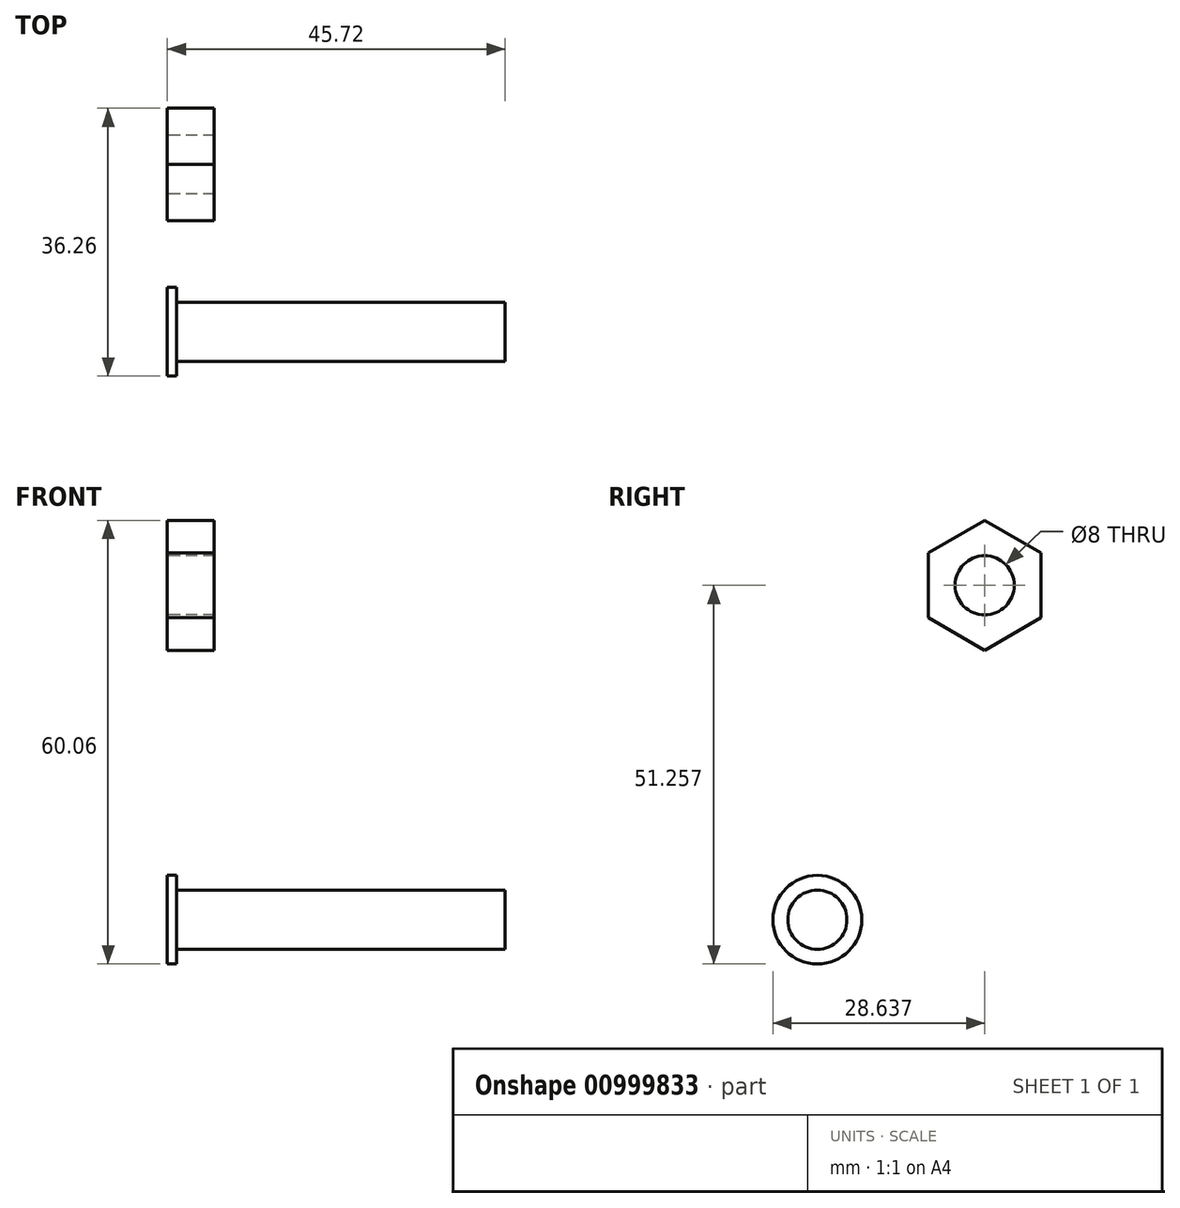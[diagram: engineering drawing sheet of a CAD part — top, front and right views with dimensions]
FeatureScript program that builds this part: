
annotation { "Feature Type Name" : "Feature", "Feature Type Description" : "" }
export const myFeature = defineFeature(function(context is Context, id is Id, definition is map)
    precondition{}
    {
        {
            var Q0;
            Q0=qCreatedBy(makeId("Right.planeOp"),FACE);
            var sketch = newSketch(context, id + "F0", { "sketchPlane" : qUnion([Q0])});
            skCircle(sketch, "E0", {"center": v(0, 0) * mm, "radius": 4 * mm});
            skCircle(sketch, "E1", {"center": v(0, 0) * mm, "radius": 6 * mm});
            skSolve(sketch);
        }
        {
            var Q0;
            Q0=makeQuery(id+"F0.imprint","IMPRINT",FACE,{"disambiguationData":[TD([[makeQuery(id+"F0.imprint","IMPRINT",EDGE,{"derivedFrom":sQuery(id+"F0.wireOp",EDGE,"E0")}),1.0]])]});
            extrude(context, id + "F1", {"entities" : qUnion([Q0]), "depth" : 45.72 * mm, "offsetDistance" : 25.4 * mm});
        }
        {
            var Q0;
            Q0 = qSketchRegion(id + "F0", true);
            extrude(context, id + "F2", {"entities" : qUnion([Q0]), "operationType" : NewBodyOperationType.ADD, "depth" : 1.27 * mm, "offsetDistance" : 25.4 * mm});
        }
        {
            var Q0;
            Q0=qCreatedBy(makeId("Right.planeOp"),FACE);
            var sketch = newSketch(context, id + "F3", { "sketchPlane" : qUnion([Q0])});
            skCircle(sketch, "E2.cCircle", {"center": v(22.64, 45.26) * mm, "radius": 7.62 * mm, "construction": true});
            skLineSegment(sketch, "E2.0", {"start": v(30.26, 49.66) * mm, "end": v(30.26, 40.86) * mm});
            skLineSegment(sketch, "E2.1", {"start": v(30.26, 40.86) * mm, "end": v(22.64, 36.46) * mm});
            skLineSegment(sketch, "E2.2", {"start": v(22.64, 36.46) * mm, "end": v(15.02, 40.86) * mm});
            skLineSegment(sketch, "E2.3", {"start": v(15.02, 40.86) * mm, "end": v(15.02, 49.66) * mm});
            skLineSegment(sketch, "E2.4", {"start": v(15.02, 49.66) * mm, "end": v(22.64, 54.06) * mm});
            skLineSegment(sketch, "E2.5", {"start": v(22.64, 54.06) * mm, "end": v(30.26, 49.66) * mm});
            skPoint(sketch, "E2.0.midPoint", {"position": v(30.26, 45.26) * mm});
            skCircle(sketch, "E3", {"center": v(22.64, 45.26) * mm, "radius": 4 * mm});
            skSolve(sketch);
        }
        {
            var Q0;
            Q0=makeQuery(id+"F3.imprint","IMPRINT",FACE,{"disambiguationData":[TD([[makeQuery(id+"F3.imprint","IMPRINT",EDGE,{"derivedFrom":sQuery(id+"F3.wireOp",EDGE,"E2.0")}),-1.0]])]});
            extrude(context, id + "F4", {"entities" : qUnion([Q0]), "depth" : 6.35 * mm, "offsetDistance" : 25.4 * mm});
        }
    });
